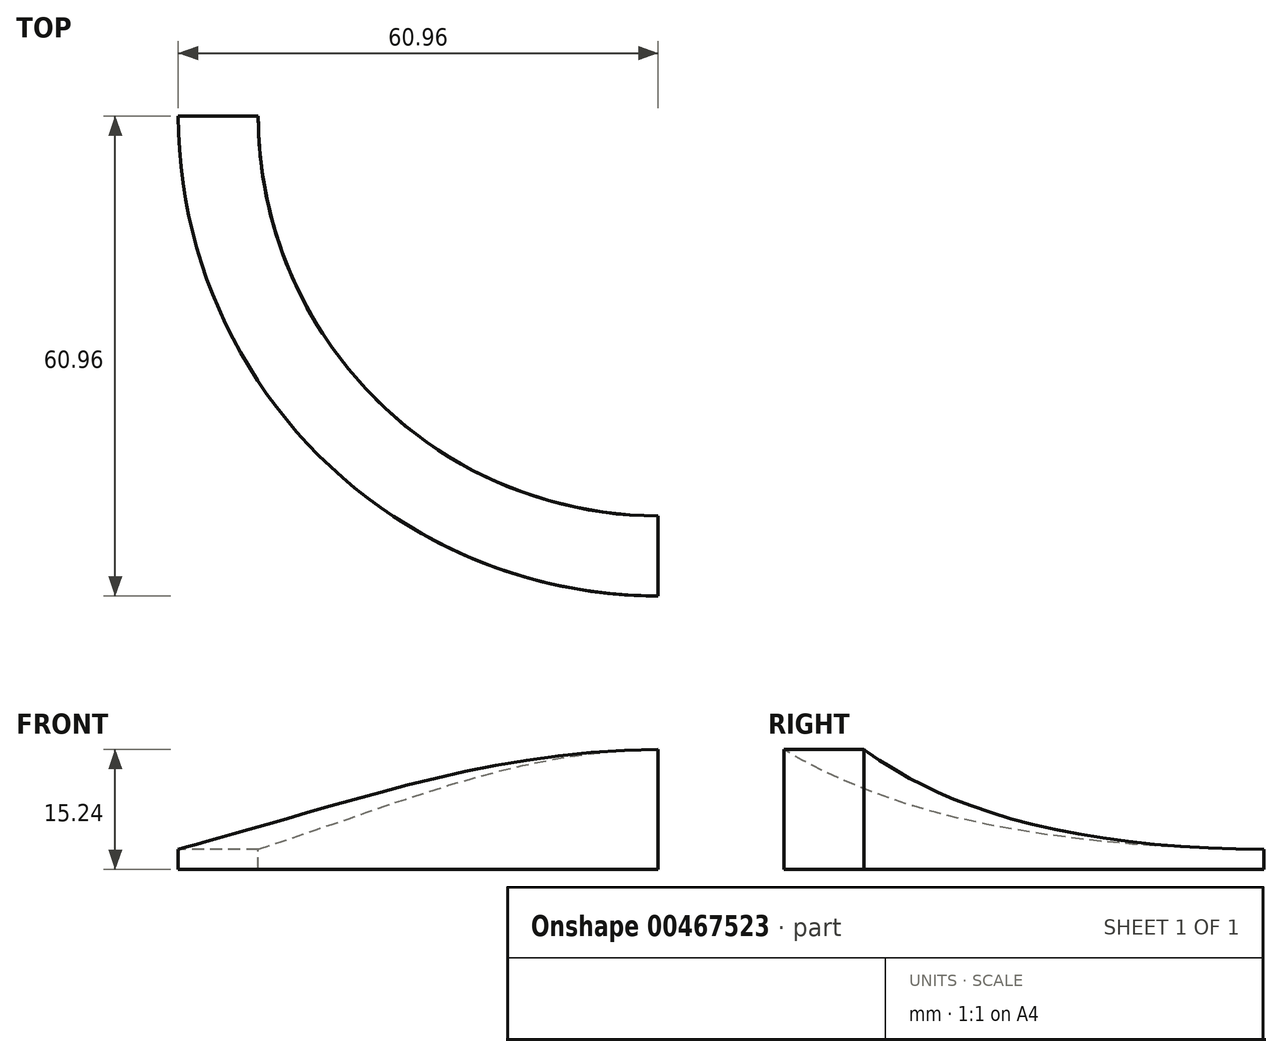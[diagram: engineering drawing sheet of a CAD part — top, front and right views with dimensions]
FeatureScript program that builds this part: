
annotation { "Feature Type Name" : "Feature", "Feature Type Description" : "" }
export const myFeature = defineFeature(function(context is Context, id is Id, definition is map)
    precondition{}
    {
        {
            var Q0;
            Q0=qCreatedBy(makeId("Front.planeOp"),FACE);
            var sketch = newSketch(context, id + "F0", { "sketchPlane" : qUnion([Q0])});
            skLineSegment(sketch, "E0", {"start": v(0, 0) * mm, "end": v(-50.8, 0) * mm, "construction": true});
            skLineSegment(sketch, "E1.bottom", {"start": v(-50.8, 0) * mm, "end": v(-60.96, 0) * mm});
            skLineSegment(sketch, "E1.top", {"start": v(-50.8, 2.54) * mm, "end": v(-60.96, 2.54) * mm});
            skLineSegment(sketch, "E1.left", {"start": v(-50.8, 0) * mm, "end": v(-50.8, 2.54) * mm});
            skLineSegment(sketch, "E1.right", {"start": v(-60.96, 0) * mm, "end": v(-60.96, 2.54) * mm});
            skSolve(sketch);
        }
        {
            var Q0;
            Q0=qCreatedBy(makeId("Front.planeOp"),FACE);
            var sketch = newSketch(context, id + "F1", { "sketchPlane" : qUnion([Q0])});
            skLineSegment(sketch, "E2", {"start": v(0, 0) * mm, "end": v(0, 30.25) * mm, "construction": true});
            skSolve(sketch);
        }
        {
            var Q0;
            Q0=qCreatedBy(makeId("Front.planeOp"),FACE);
            var Q1;
            Q1=sQuery(id+"F1.wireOp",EDGE,"E2");
            cPlane(context, id + "F2", {"entities" : qUnion([Q0, Q1]), "cplaneType" : CPlaneType.LINE_ANGLE, "offset" : 25.4 * mm, "angle" : 45 * degree, "width" : 152.4 * mm, "height" : 152.4 * mm});
        }
        {
            var Q0;
            Q0=qCreatedBy(id+"F2.planeOp",FACE);
            var sketch = newSketch(context, id + "F3", { "sketchPlane" : qUnion([Q0])});
            skLineSegment(sketch, "E3", {"start": v(0, 0) * mm, "end": v(50.8, 0) * mm, "construction": true});
            skLineSegment(sketch, "E4.bottom", {"start": v(50.8, 0) * mm, "end": v(60.96, 0) * mm});
            skLineSegment(sketch, "E4.top", {"start": v(50.8, 7.62) * mm, "end": v(60.96, 7.62) * mm});
            skLineSegment(sketch, "E4.left", {"start": v(50.8, 0) * mm, "end": v(50.8, 7.62) * mm});
            skLineSegment(sketch, "E4.right", {"start": v(60.96, 0) * mm, "end": v(60.96, 7.62) * mm});
            skSolve(sketch);
        }
        {
            var Q0;
            Q0=qCreatedBy(makeId("Right.planeOp"),FACE);
            var sketch = newSketch(context, id + "F4", { "sketchPlane" : qUnion([Q0])});
            skLineSegment(sketch, "E5", {"start": v(0, 0) * mm, "end": v(-50.8, 0) * mm, "construction": true});
            skLineSegment(sketch, "E6.bottom", {"start": v(-50.8, 0) * mm, "end": v(-60.96, 0) * mm});
            skLineSegment(sketch, "E6.top", {"start": v(-50.8, 15.24) * mm, "end": v(-60.96, 15.24) * mm});
            skLineSegment(sketch, "E6.left", {"start": v(-50.8, 0) * mm, "end": v(-50.8, 15.24) * mm});
            skLineSegment(sketch, "E6.right", {"start": v(-60.96, 0) * mm, "end": v(-60.96, 15.24) * mm});
            skSolve(sketch);
        }
        {
            var Q0;
            Q0=makeQuery(id+"F0.imprint","IMPRINT",FACE,{"disambiguationData":[TD([[makeQuery(id+"F0.imprint","IMPRINT",EDGE,{"derivedFrom":sQuery(id+"F0.wireOp",EDGE,"E1.bottom")}),-1.0]])]});
            var Q1;
            Q1=makeQuery(id+"F3.imprint","IMPRINT",FACE,{"disambiguationData":[TD([[makeQuery(id+"F3.imprint","IMPRINT",EDGE,{"derivedFrom":sQuery(id+"F3.wireOp",EDGE,"E4.bottom")}),1.0]])]});
            var Q2;
            Q2=makeQuery(id+"F4.imprint","IMPRINT",FACE,{"disambiguationData":[TD([[makeQuery(id+"F4.imprint","IMPRINT",EDGE,{"derivedFrom":sQuery(id+"F4.wireOp",EDGE,"E6.bottom")}),-1.0]])]});
            loft(context, id + "F5", {"startCondition" : LoftEndDerivativeType.NORMAL_TO_PROFILE, "startMagnitude" : 1, "endCondition" : LoftEndDerivativeType.NORMAL_TO_PROFILE, "endMagnitude" : 1, "sheetProfilesArray" : [{ "sheetProfileEntities" : qUnion([Q0]) }, { "sheetProfileEntities" : qUnion([Q1]) }, { "sheetProfileEntities" : qUnion([Q2]) }]});
        }
    });
